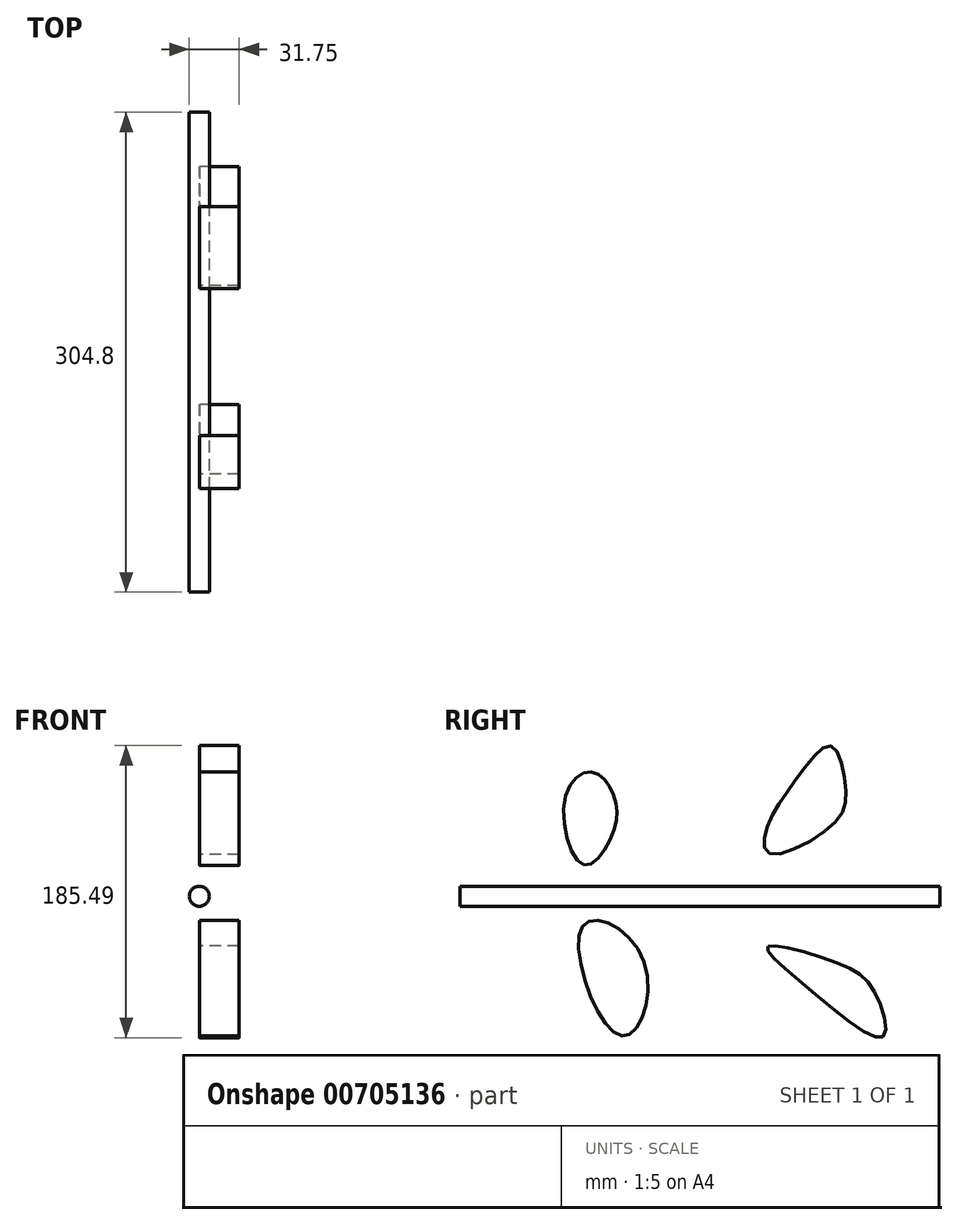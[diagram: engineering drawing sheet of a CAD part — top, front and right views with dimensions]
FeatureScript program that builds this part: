
annotation { "Feature Type Name" : "Feature", "Feature Type Description" : "" }
export const myFeature = defineFeature(function(context is Context, id is Id, definition is map)
    precondition{}
    {
        {
            var Q0;
            Q0=qCreatedBy(makeId("Front.planeOp"),FACE);
            var sketch = newSketch(context, id + "F0", { "sketchPlane" : qUnion([Q0])});
            skCircle(sketch, "E0", {"center": v(0, 0) * mm, "radius": 6.35 * mm});
            skSolve(sketch);
        }
        {
            var Q0;
            Q0 = qSketchRegion(id + "F0", true);
            extrude(context, id + "F1", {"entities" : qUnion([Q0]), "endBound" : BoundingType.SYMMETRIC, "depth" : 304.8 * mm, "offsetDistance" : 25.4 * mm});
        }
        {
            var Q0;
            Q0=qCreatedBy(makeId("Right.planeOp"),FACE);
            var sketch = newSketch(context, id + "F2", { "sketchPlane" : qUnion([Q0])});
            skFitSpline(sketch, "E1", {"points": [v(-74.75, -19.17) * mm, v(-36.06, -40.58) * mm, v(-50.59, -88.58) * mm, v(-74.75, -19.17) * mm]});
            skFitSpline(sketch, "E2", {"points": [v(-73.74, 19.86) * mm, v(-55.77, 39.2) * mm, v(-54.74, 63.71) * mm, v(-68.55, 78.9) * mm, v(-85.83, 62.33) * mm, v(-73.74, 19.86) * mm]});
            skFitSpline(sketch, "E3", {"points": [v(43.03, -31.94) * mm, v(63.76, -54.39) * mm, v(115.95, -89.27) * mm, v(111.1, -61.3) * mm, v(86.56, -42.3) * mm, v(43.03, -31.94) * mm]});
            skFitSpline(sketch, "E4", {"points": [v(44.07, 27.1) * mm, v(84.14, 45.41) * mm, v(92.44, 68.55) * mm, v(83.1, 95.48) * mm, v(61.69, 75.1) * mm, v(42.34, 43.34) * mm, v(44.07, 27.1) * mm]});
            skSolve(sketch);
        }
        {
            var Q0;
            Q0 = qSketchRegion(id + "F2", true);
            extrude(context, id + "F3", {"entities" : qUnion([Q0]), "depth" : 25.4 * mm, "offsetDistance" : 25.4 * mm});
        }
    });
